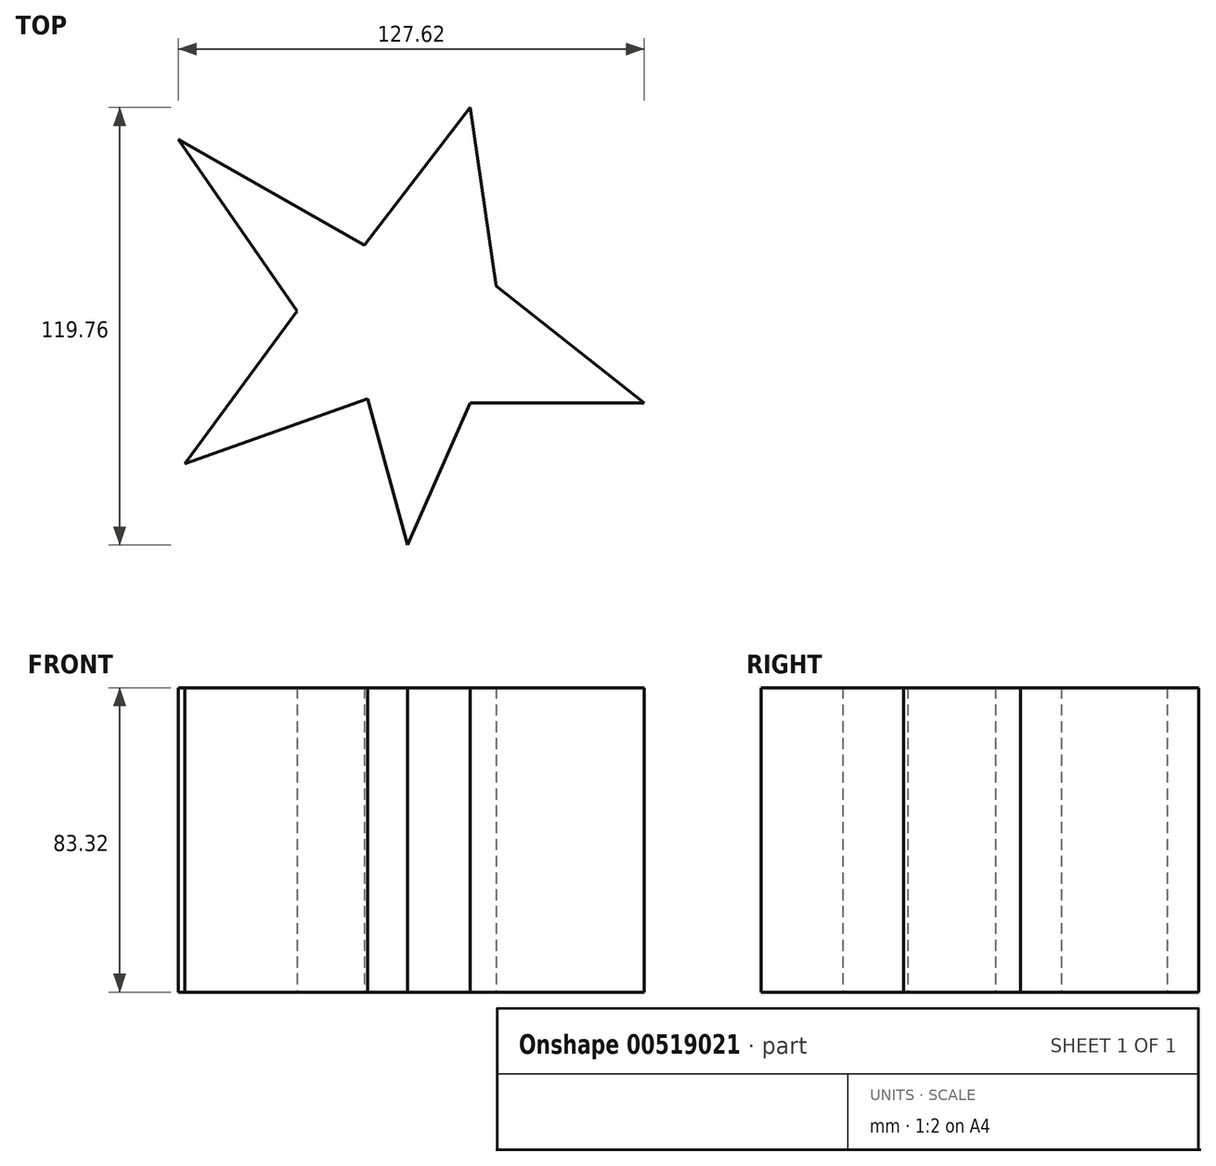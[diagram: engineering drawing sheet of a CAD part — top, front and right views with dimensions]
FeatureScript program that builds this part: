
annotation { "Feature Type Name" : "Feature", "Feature Type Description" : "" }
export const myFeature = defineFeature(function(context is Context, id is Id, definition is map)
    precondition{}
    {
        {
            var Q0;
            Q0=qCreatedBy(makeId("Top.planeOp"),FACE);
            var sketch = newSketch(context, id + "F0", { "sketchPlane" : qUnion([Q0])});
            skLineSegment(sketch, "E0", {"start": v(0, 0) * mm, "end": v(17.19, 38.97) * mm});
            skLineSegment(sketch, "E1", {"start": v(17.19, 38.97) * mm, "end": v(64.88, 38.97) * mm});
            skLineSegment(sketch, "E2", {"start": v(64.88, 38.97) * mm, "end": v(24.28, 70.9) * mm});
            skLineSegment(sketch, "E3", {"start": v(24.28, 70.9) * mm, "end": v(17.19, 119.76) * mm});
            skLineSegment(sketch, "E4", {"start": v(17.19, 119.76) * mm, "end": v(-11.71, 82.1) * mm});
            skLineSegment(sketch, "E5", {"start": v(-11.71, 82.1) * mm, "end": v(-62.74, 111.07) * mm});
            skLineSegment(sketch, "E6", {"start": v(-62.74, 111.07) * mm, "end": v(-30.12, 64.07) * mm});
            skLineSegment(sketch, "E7", {"start": v(-30.12, 64.07) * mm, "end": v(-60.94, 22.3) * mm});
            skLineSegment(sketch, "E8", {"start": v(-60.94, 22.3) * mm, "end": v(-10.81, 40.06) * mm});
            skLineSegment(sketch, "E9", {"start": v(-10.81, 40.06) * mm, "end": v(0, 0) * mm});
            skSolve(sketch);
        }
        {
            var Q0;
            Q0 = qSketchRegion(id + "F0", true);
            extrude(context, id + "F1", {"entities" : qUnion([Q0]), "endBound" : BoundingType.SYMMETRIC, "depth" : 83.31 * mm, "offsetDistance" : 25.4 * mm});
        }
    });
